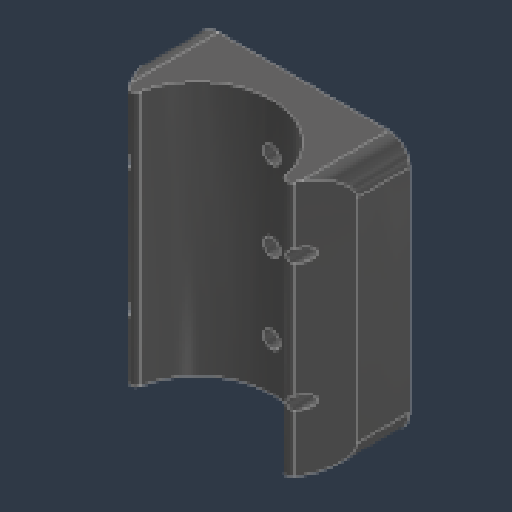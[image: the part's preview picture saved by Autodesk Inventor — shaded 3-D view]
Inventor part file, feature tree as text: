
AUTODESK INVENTOR PART (.ipt)
format: ipt  version: 2024.3 (Build 283343000, 343)  size: 174,592 bytes
history: native  units: mm (DEFAULTED — no unit token found)
features: sketch x4, extrude x2, fillet x2, hole x2, projected_geometry x1
ambient origin geometry x8: Origin, YZ Plane, XZ Plane, XY Plane, X Axis, Y Axis, Z Axis, Center Point
bodies: Solid1 (feature_tree)
feature tree (11):
  extrude  "Extrusion1"  Depth=76.2mm
  extrude  "Extrusion2"  Depth=6.35mm
  fillet  "Fillet1"  Radius=6.35mm
  hole  "Hole2"  [1 undecoded]
  hole  "Hole3"  [1 undecoded]
  fillet  "Fillet3"  Radius=50.8mm
  sketch  "Sketch2"  dims[d0=63.5mm d1=76.2mm]
  sketch  "Sketch4"  dims[d2=31.75mm d3=0.0mm d11=44.45mm d12=6.35mm]
  projected_geometry  "Projected Loop1"
  sketch  "Sketch5"  dims[d13=0.0mm d14=0.0mm d15=1.5875mm]
  sketch  "Sketch6"  dims[d16=15.875mm d17=38.1mm d18=50.8mm d19=3.9624mm d20=9.652mm d21=9.525mm d22=6.35mm d23=14.3117mm d24=25.4mm d25=20.594885mm d26=5.1054mm d27=9.652mm d28=9.525mm d29=4.826mm d30=14.3117mm d31=25.4mm d32=20.594885mm d34=6.35mm]
note: 2 required parameter values undecoded (feature->parameter linkage not recoverable at this tier; creation-order binding heuristic only, values carry confidence <= 0.55)
